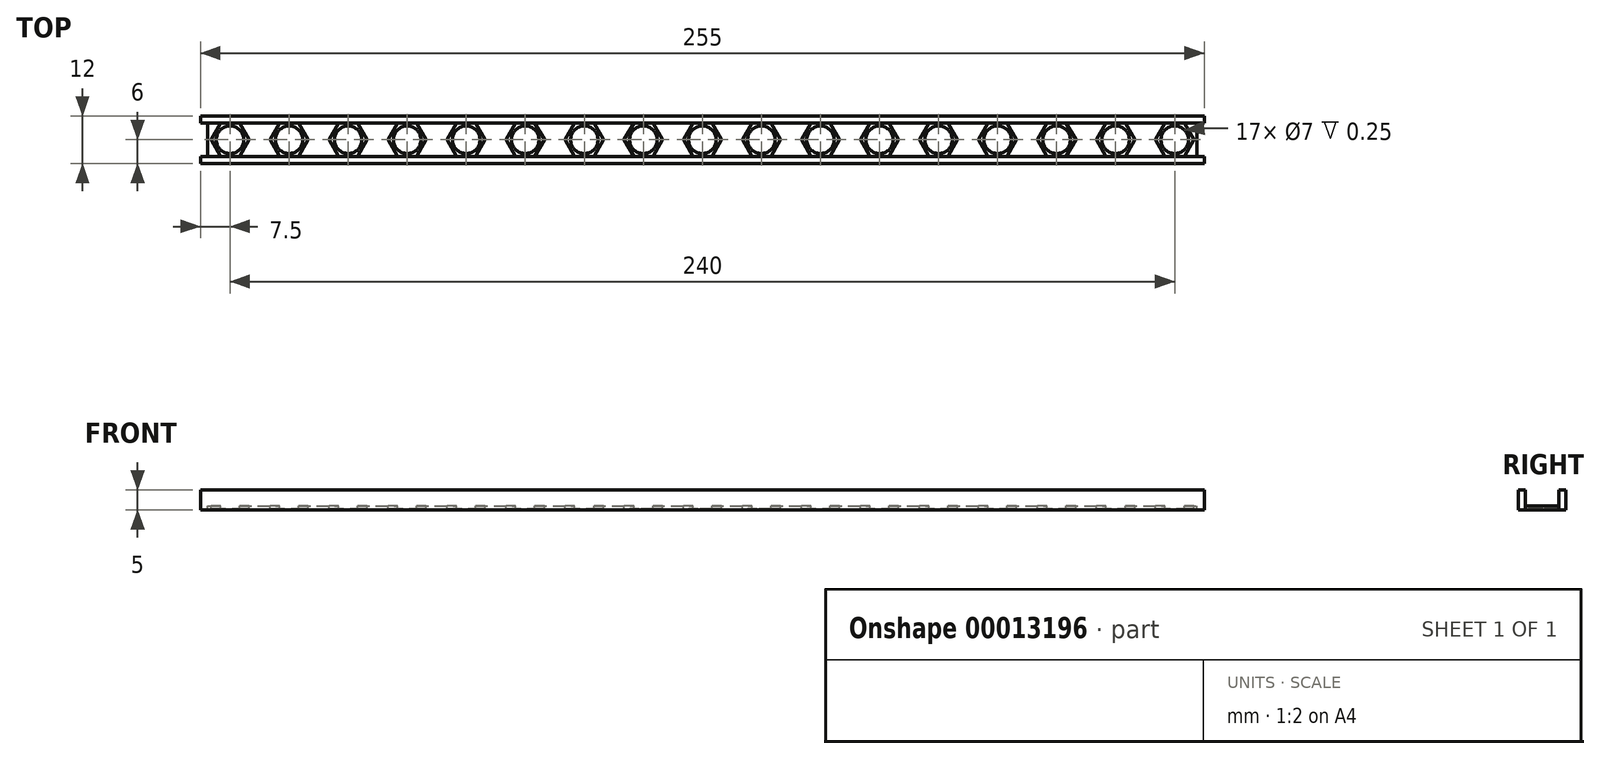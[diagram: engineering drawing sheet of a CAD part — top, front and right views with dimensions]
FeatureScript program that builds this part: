
annotation { "Feature Type Name" : "Feature", "Feature Type Description" : "" }
export const myFeature = defineFeature(function(context is Context, id is Id, definition is map)
    precondition{}
    {
        {
            var Q0;
            Q0=qCreatedBy(makeId("Top.planeOp"),FACE);
            var sketch = newSketch(context, id + "F0", { "sketchPlane" : qUnion([Q0])});
            skLineSegment(sketch, "E0.bottom", {"start": v(-127.5, 6) * mm, "end": v(127.5, 6) * mm});
            skLineSegment(sketch, "E0.top", {"start": v(-127.5, -6) * mm, "end": v(127.5, -6) * mm});
            skLineSegment(sketch, "E0.left", {"start": v(-127.5, 6) * mm, "end": v(-127.5, -6) * mm});
            skLineSegment(sketch, "E0.right", {"start": v(127.5, 6) * mm, "end": v(127.5, -6) * mm});
            skLineSegment(sketch, "E1", {"start": v(0, 0) * mm, "end": v(0, -6) * mm, "construction": true});
            skLineSegment(sketch, "E2", {"start": v(0, 0) * mm, "end": v(127.5, 0) * mm, "construction": true});
            skCircle(sketch, "E3.cCircle", {"center": v(0, 0) * mm, "radius": 4.2 * mm, "construction": true});
            skLineSegment(sketch, "E3.0", {"start": v(2.42, -4.2) * mm, "end": v(-2.42, -4.2) * mm});
            skLineSegment(sketch, "E3.1", {"start": v(-2.42, -4.2) * mm, "end": v(-4.85, 0) * mm});
            skLineSegment(sketch, "E3.2", {"start": v(-4.85, 0) * mm, "end": v(-2.42, 4.2) * mm});
            skLineSegment(sketch, "E3.3", {"start": v(-2.42, 4.2) * mm, "end": v(2.42, 4.2) * mm});
            skLineSegment(sketch, "E3.4", {"start": v(2.42, 4.2) * mm, "end": v(4.85, 0) * mm});
            skLineSegment(sketch, "E3.5", {"start": v(4.85, 0) * mm, "end": v(2.42, -4.2) * mm});
            skPoint(sketch, "E3.0.midPoint", {"position": v(0, -4.2) * mm});
            skCircle(sketch, "E4.cCircle", {"center": v(15, 0) * mm, "radius": 4.2 * mm, "construction": true});
            skLineSegment(sketch, "E4.0", {"start": v(17.42, -4.2) * mm, "end": v(12.58, -4.2) * mm});
            skLineSegment(sketch, "E4.1", {"start": v(12.58, -4.2) * mm, "end": v(10.15, 0) * mm});
            skLineSegment(sketch, "E4.2", {"start": v(10.15, 0) * mm, "end": v(12.58, 4.2) * mm});
            skLineSegment(sketch, "E4.3", {"start": v(12.58, 4.2) * mm, "end": v(17.42, 4.2) * mm});
            skLineSegment(sketch, "E4.4", {"start": v(17.42, 4.2) * mm, "end": v(19.85, 0) * mm});
            skLineSegment(sketch, "E4.5", {"start": v(19.85, 0) * mm, "end": v(17.42, -4.2) * mm});
            skPoint(sketch, "E4.0.midPoint", {"position": v(15, -4.2) * mm});
            skCircle(sketch, "E5.cCircle", {"center": v(-15, 0) * mm, "radius": 4.2 * mm, "construction": true});
            skLineSegment(sketch, "E5.0", {"start": v(-12.58, -4.2) * mm, "end": v(-17.42, -4.2) * mm});
            skLineSegment(sketch, "E5.1", {"start": v(-17.42, -4.2) * mm, "end": v(-19.85, 0) * mm});
            skLineSegment(sketch, "E5.2", {"start": v(-19.85, 0) * mm, "end": v(-17.42, 4.2) * mm});
            skLineSegment(sketch, "E5.3", {"start": v(-17.42, 4.2) * mm, "end": v(-12.58, 4.2) * mm});
            skLineSegment(sketch, "E5.4", {"start": v(-12.58, 4.2) * mm, "end": v(-10.15, 0) * mm});
            skLineSegment(sketch, "E5.5", {"start": v(-10.15, 0) * mm, "end": v(-12.58, -4.2) * mm});
            skPoint(sketch, "E5.0.midPoint", {"position": v(-15, -4.2) * mm});
            skLineSegment(sketch, "E6", {"start": v(-15, 0) * mm, "end": v(0, 0) * mm, "construction": true});
            skLineSegment(sketch, "E7", {"start": v(0, 0) * mm, "end": v(15, 0) * mm, "construction": true});
            skCircle(sketch, "E8", {"center": v(-15, 0) * mm, "radius": 3.5 * mm});
            skCircle(sketch, "E9", {"center": v(0, 0) * mm, "radius": 3.5 * mm});
            skCircle(sketch, "E10", {"center": v(15, 0) * mm, "radius": 3.5 * mm});
            skLineSegment(sketch, "E11.top", {"start": v(-127.5, 4.2) * mm, "end": v(127.5, 4.2) * mm});
            skLineSegment(sketch, "E11.left", {"start": v(-127.5, 6) * mm, "end": v(-127.5, 4.2) * mm});
            skLineSegment(sketch, "E11.right", {"start": v(127.5, 6) * mm, "end": v(127.5, 4.2) * mm});
            skLineSegment(sketch, "E12.top", {"start": v(-127.5, -4.2) * mm, "end": v(127.5, -4.2) * mm});
            skLineSegment(sketch, "E12.left", {"start": v(-127.5, -6) * mm, "end": v(-127.5, -4.2) * mm});
            skLineSegment(sketch, "E12.right", {"start": v(127.5, -6) * mm, "end": v(127.5, -4.2) * mm});
            skLineSegment(sketch, "E13.bottom", {"start": v(-127.5, 4.2) * mm, "end": v(-125.7, 4.2) * mm});
            skLineSegment(sketch, "E13.top", {"start": v(-127.5, -4.2) * mm, "end": v(-125.7, -4.2) * mm});
            skLineSegment(sketch, "E13.left", {"start": v(-127.5, 4.2) * mm, "end": v(-127.5, -4.2) * mm});
            skLineSegment(sketch, "E13.right", {"start": v(-125.7, 4.2) * mm, "end": v(-125.7, -4.2) * mm});
            skLineSegment(sketch, "E14.bottom", {"start": v(127.5, 4.2) * mm, "end": v(125.7, 4.2) * mm});
            skLineSegment(sketch, "E14.top", {"start": v(127.5, -4.2) * mm, "end": v(125.7, -4.2) * mm});
            skLineSegment(sketch, "E14.left", {"start": v(127.5, 4.2) * mm, "end": v(127.5, -4.2) * mm});
            skLineSegment(sketch, "E14.right", {"start": v(125.7, 4.2) * mm, "end": v(125.7, -4.2) * mm});
            skLineSegment(sketch, "E15.1", {"start": v(-32.42, -4.2) * mm, "end": v(-34.85, 0) * mm});
            skCircle(sketch, "E15.cCircle", {"center": v(-30, 0) * mm, "radius": 4.2 * mm, "construction": true});
            skPoint(sketch, "E15.0.midPoint", {"position": v(-30, -4.2) * mm});
            skLineSegment(sketch, "E15.4", {"start": v(-27.58, 4.2) * mm, "end": v(-25.15, 0) * mm});
            skLineSegment(sketch, "E15.2", {"start": v(-34.85, 0) * mm, "end": v(-32.42, 4.2) * mm});
            skLineSegment(sketch, "E15.0", {"start": v(-27.58, -4.2) * mm, "end": v(-32.42, -4.2) * mm});
            skLineSegment(sketch, "E15.3", {"start": v(-32.42, 4.2) * mm, "end": v(-27.58, 4.2) * mm});
            skLineSegment(sketch, "E15.5", {"start": v(-25.15, 0) * mm, "end": v(-27.58, -4.2) * mm});
            skCircle(sketch, "E16", {"center": v(-30, 0) * mm, "radius": 3.5 * mm});
            skLineSegment(sketch, "E17", {"start": v(-30, 0) * mm, "end": v(-15, 0) * mm, "construction": true});
            skLineSegment(sketch, "E18.1", {"start": v(-47.42, -4.2) * mm, "end": v(-49.85, 0) * mm});
            skCircle(sketch, "E18.cCircle", {"center": v(-45, 0) * mm, "radius": 4.2 * mm, "construction": true});
            skPoint(sketch, "E18.0.midPoint", {"position": v(-45, -4.2) * mm});
            skLineSegment(sketch, "E18.4", {"start": v(-42.58, 4.2) * mm, "end": v(-40.15, 0) * mm});
            skLineSegment(sketch, "E18.2", {"start": v(-49.85, 0) * mm, "end": v(-47.42, 4.2) * mm});
            skLineSegment(sketch, "E18.0", {"start": v(-42.58, -4.2) * mm, "end": v(-47.42, -4.2) * mm});
            skLineSegment(sketch, "E18.3", {"start": v(-47.42, 4.2) * mm, "end": v(-42.58, 4.2) * mm});
            skLineSegment(sketch, "E18.5", {"start": v(-40.15, 0) * mm, "end": v(-42.58, -4.2) * mm});
            skCircle(sketch, "E19", {"center": v(-45, 0) * mm, "radius": 3.5 * mm});
            skLineSegment(sketch, "E20", {"start": v(-45, 0) * mm, "end": v(-30, 0) * mm, "construction": true});
            skLineSegment(sketch, "E21.1", {"start": v(-62.42, -4.2) * mm, "end": v(-64.85, 0) * mm});
            skCircle(sketch, "E21.cCircle", {"center": v(-60, 0) * mm, "radius": 4.2 * mm, "construction": true});
            skPoint(sketch, "E21.0.midPoint", {"position": v(-60, -4.2) * mm});
            skLineSegment(sketch, "E21.4", {"start": v(-57.58, 4.2) * mm, "end": v(-55.15, 0) * mm});
            skLineSegment(sketch, "E21.2", {"start": v(-64.85, 0) * mm, "end": v(-62.42, 4.2) * mm});
            skLineSegment(sketch, "E21.0", {"start": v(-57.58, -4.2) * mm, "end": v(-62.42, -4.2) * mm});
            skLineSegment(sketch, "E21.3", {"start": v(-62.42, 4.2) * mm, "end": v(-57.58, 4.2) * mm});
            skLineSegment(sketch, "E21.5", {"start": v(-55.15, 0) * mm, "end": v(-57.58, -4.2) * mm});
            skCircle(sketch, "E22", {"center": v(-60, 0) * mm, "radius": 3.5 * mm});
            skLineSegment(sketch, "E23", {"start": v(-60, 0) * mm, "end": v(-45, 0) * mm, "construction": true});
            skLineSegment(sketch, "E24.1", {"start": v(-77.42, -4.2) * mm, "end": v(-79.85, 0) * mm});
            skCircle(sketch, "E24.cCircle", {"center": v(-75, 0) * mm, "radius": 4.2 * mm, "construction": true});
            skPoint(sketch, "E24.0.midPoint", {"position": v(-75, -4.2) * mm});
            skLineSegment(sketch, "E24.4", {"start": v(-72.58, 4.2) * mm, "end": v(-70.15, 0) * mm});
            skLineSegment(sketch, "E24.2", {"start": v(-79.85, 0) * mm, "end": v(-77.42, 4.2) * mm});
            skLineSegment(sketch, "E24.0", {"start": v(-72.58, -4.2) * mm, "end": v(-77.42, -4.2) * mm});
            skLineSegment(sketch, "E24.3", {"start": v(-77.42, 4.2) * mm, "end": v(-72.58, 4.2) * mm});
            skLineSegment(sketch, "E24.5", {"start": v(-70.15, 0) * mm, "end": v(-72.58, -4.2) * mm});
            skCircle(sketch, "E25", {"center": v(-75, 0) * mm, "radius": 3.5 * mm});
            skLineSegment(sketch, "E26", {"start": v(-75, 0) * mm, "end": v(-60, 0) * mm, "construction": true});
            skLineSegment(sketch, "E27.1", {"start": v(-92.42, -4.2) * mm, "end": v(-94.85, 0) * mm});
            skCircle(sketch, "E27.cCircle", {"center": v(-90, 0) * mm, "radius": 4.2 * mm, "construction": true});
            skPoint(sketch, "E27.0.midPoint", {"position": v(-90, -4.2) * mm});
            skLineSegment(sketch, "E27.4", {"start": v(-87.58, 4.2) * mm, "end": v(-85.15, 0) * mm});
            skLineSegment(sketch, "E27.2", {"start": v(-94.85, 0) * mm, "end": v(-92.42, 4.2) * mm});
            skLineSegment(sketch, "E27.0", {"start": v(-87.58, -4.2) * mm, "end": v(-92.42, -4.2) * mm});
            skLineSegment(sketch, "E27.3", {"start": v(-92.42, 4.2) * mm, "end": v(-87.58, 4.2) * mm});
            skLineSegment(sketch, "E27.5", {"start": v(-85.15, 0) * mm, "end": v(-87.58, -4.2) * mm});
            skCircle(sketch, "E28", {"center": v(-90, 0) * mm, "radius": 3.5 * mm});
            skLineSegment(sketch, "E29", {"start": v(-90, 0) * mm, "end": v(-75, 0) * mm, "construction": true});
            skLineSegment(sketch, "E30.1", {"start": v(-107.42, -4.2) * mm, "end": v(-109.85, 0) * mm});
            skCircle(sketch, "E30.cCircle", {"center": v(-105, 0) * mm, "radius": 4.2 * mm, "construction": true});
            skPoint(sketch, "E30.0.midPoint", {"position": v(-105, -4.2) * mm});
            skLineSegment(sketch, "E30.4", {"start": v(-102.58, 4.2) * mm, "end": v(-100.15, 0) * mm});
            skLineSegment(sketch, "E30.2", {"start": v(-109.85, 0) * mm, "end": v(-107.42, 4.2) * mm});
            skLineSegment(sketch, "E30.0", {"start": v(-102.58, -4.2) * mm, "end": v(-107.42, -4.2) * mm});
            skLineSegment(sketch, "E30.3", {"start": v(-107.42, 4.2) * mm, "end": v(-102.58, 4.2) * mm});
            skLineSegment(sketch, "E30.5", {"start": v(-100.15, 0) * mm, "end": v(-102.58, -4.2) * mm});
            skCircle(sketch, "E31", {"center": v(-105, 0) * mm, "radius": 3.5 * mm});
            skLineSegment(sketch, "E32", {"start": v(-105, 0) * mm, "end": v(-90, 0) * mm, "construction": true});
            skLineSegment(sketch, "E33.1", {"start": v(-122.42, -4.2) * mm, "end": v(-124.85, 0) * mm});
            skCircle(sketch, "E33.cCircle", {"center": v(-120, 0) * mm, "radius": 4.2 * mm, "construction": true});
            skPoint(sketch, "E33.0.midPoint", {"position": v(-120, -4.2) * mm});
            skLineSegment(sketch, "E33.4", {"start": v(-117.58, 4.2) * mm, "end": v(-115.15, 0) * mm});
            skLineSegment(sketch, "E33.2", {"start": v(-124.85, 0) * mm, "end": v(-122.42, 4.2) * mm});
            skLineSegment(sketch, "E33.0", {"start": v(-117.58, -4.2) * mm, "end": v(-122.42, -4.2) * mm});
            skLineSegment(sketch, "E33.3", {"start": v(-122.42, 4.2) * mm, "end": v(-117.58, 4.2) * mm});
            skLineSegment(sketch, "E33.5", {"start": v(-115.15, 0) * mm, "end": v(-117.58, -4.2) * mm});
            skCircle(sketch, "E34", {"center": v(-120, 0) * mm, "radius": 3.5 * mm});
            skLineSegment(sketch, "E35", {"start": v(-120, 0) * mm, "end": v(-105, 0) * mm, "construction": true});
            skLineSegment(sketch, "E36.1", {"start": v(27.58, -4.2) * mm, "end": v(25.15, 0) * mm});
            skCircle(sketch, "E36.cCircle", {"center": v(30, 0) * mm, "radius": 4.2 * mm, "construction": true});
            skPoint(sketch, "E36.0.midPoint", {"position": v(30, -4.2) * mm});
            skLineSegment(sketch, "E36.4", {"start": v(32.42, 4.2) * mm, "end": v(34.85, 0) * mm});
            skLineSegment(sketch, "E36.2", {"start": v(25.15, 0) * mm, "end": v(27.58, 4.2) * mm});
            skLineSegment(sketch, "E36.0", {"start": v(32.42, -4.2) * mm, "end": v(27.58, -4.2) * mm});
            skLineSegment(sketch, "E36.3", {"start": v(27.58, 4.2) * mm, "end": v(32.42, 4.2) * mm});
            skLineSegment(sketch, "E36.5", {"start": v(34.85, 0) * mm, "end": v(32.42, -4.2) * mm});
            skCircle(sketch, "E37", {"center": v(30, 0) * mm, "radius": 3.5 * mm});
            skLineSegment(sketch, "E38", {"start": v(15, 0) * mm, "end": v(30, 0) * mm, "construction": true});
            skLineSegment(sketch, "E39.1", {"start": v(42.58, -4.2) * mm, "end": v(40.15, 0) * mm});
            skCircle(sketch, "E39.cCircle", {"center": v(45, 0) * mm, "radius": 4.2 * mm, "construction": true});
            skPoint(sketch, "E39.0.midPoint", {"position": v(45, -4.2) * mm});
            skLineSegment(sketch, "E39.4", {"start": v(47.42, 4.2) * mm, "end": v(49.85, 0) * mm});
            skLineSegment(sketch, "E39.2", {"start": v(40.15, 0) * mm, "end": v(42.58, 4.2) * mm});
            skLineSegment(sketch, "E39.0", {"start": v(47.42, -4.2) * mm, "end": v(42.58, -4.2) * mm});
            skLineSegment(sketch, "E39.3", {"start": v(42.58, 4.2) * mm, "end": v(47.42, 4.2) * mm});
            skLineSegment(sketch, "E39.5", {"start": v(49.85, 0) * mm, "end": v(47.42, -4.2) * mm});
            skCircle(sketch, "E40", {"center": v(45, 0) * mm, "radius": 3.5 * mm});
            skLineSegment(sketch, "E41", {"start": v(30, 0) * mm, "end": v(45, 0) * mm, "construction": true});
            skLineSegment(sketch, "E42.1", {"start": v(57.58, -4.2) * mm, "end": v(55.15, 0) * mm});
            skCircle(sketch, "E42.cCircle", {"center": v(60, 0) * mm, "radius": 4.2 * mm, "construction": true});
            skPoint(sketch, "E42.0.midPoint", {"position": v(60, -4.2) * mm});
            skLineSegment(sketch, "E42.4", {"start": v(62.42, 4.2) * mm, "end": v(64.85, 0) * mm});
            skLineSegment(sketch, "E42.2", {"start": v(55.15, 0) * mm, "end": v(57.58, 4.2) * mm});
            skLineSegment(sketch, "E42.0", {"start": v(62.42, -4.2) * mm, "end": v(57.58, -4.2) * mm});
            skLineSegment(sketch, "E42.3", {"start": v(57.58, 4.2) * mm, "end": v(62.42, 4.2) * mm});
            skLineSegment(sketch, "E42.5", {"start": v(64.85, 0) * mm, "end": v(62.42, -4.2) * mm});
            skCircle(sketch, "E43", {"center": v(60, 0) * mm, "radius": 3.5 * mm});
            skLineSegment(sketch, "E44", {"start": v(45, 0) * mm, "end": v(60, 0) * mm, "construction": true});
            skLineSegment(sketch, "E45.1", {"start": v(72.58, -4.2) * mm, "end": v(70.15, 0) * mm});
            skCircle(sketch, "E45.cCircle", {"center": v(75, 0) * mm, "radius": 4.2 * mm, "construction": true});
            skPoint(sketch, "E45.0.midPoint", {"position": v(75, -4.2) * mm});
            skLineSegment(sketch, "E45.4", {"start": v(77.42, 4.2) * mm, "end": v(79.85, 0) * mm});
            skLineSegment(sketch, "E45.2", {"start": v(70.15, 0) * mm, "end": v(72.58, 4.2) * mm});
            skLineSegment(sketch, "E45.0", {"start": v(77.42, -4.2) * mm, "end": v(72.58, -4.2) * mm});
            skLineSegment(sketch, "E45.3", {"start": v(72.58, 4.2) * mm, "end": v(77.42, 4.2) * mm});
            skLineSegment(sketch, "E45.5", {"start": v(79.85, 0) * mm, "end": v(77.42, -4.2) * mm});
            skCircle(sketch, "E46", {"center": v(75, 0) * mm, "radius": 3.5 * mm});
            skLineSegment(sketch, "E47", {"start": v(60, 0) * mm, "end": v(75, 0) * mm, "construction": true});
            skLineSegment(sketch, "E48.1", {"start": v(87.58, -4.2) * mm, "end": v(85.15, 0) * mm});
            skCircle(sketch, "E48.cCircle", {"center": v(90, 0) * mm, "radius": 4.2 * mm, "construction": true});
            skPoint(sketch, "E48.0.midPoint", {"position": v(90, -4.2) * mm});
            skLineSegment(sketch, "E48.4", {"start": v(92.42, 4.2) * mm, "end": v(94.85, 0) * mm});
            skLineSegment(sketch, "E48.2", {"start": v(85.15, 0) * mm, "end": v(87.58, 4.2) * mm});
            skLineSegment(sketch, "E48.0", {"start": v(92.42, -4.2) * mm, "end": v(87.58, -4.2) * mm});
            skLineSegment(sketch, "E48.3", {"start": v(87.58, 4.2) * mm, "end": v(92.42, 4.2) * mm});
            skLineSegment(sketch, "E48.5", {"start": v(94.85, 0) * mm, "end": v(92.42, -4.2) * mm});
            skCircle(sketch, "E49", {"center": v(90, 0) * mm, "radius": 3.5 * mm});
            skLineSegment(sketch, "E50", {"start": v(75, 0) * mm, "end": v(90, 0) * mm, "construction": true});
            skLineSegment(sketch, "E51.1", {"start": v(102.58, -4.2) * mm, "end": v(100.15, 0) * mm});
            skCircle(sketch, "E51.cCircle", {"center": v(105, 0) * mm, "radius": 4.2 * mm, "construction": true});
            skPoint(sketch, "E51.0.midPoint", {"position": v(105, -4.2) * mm});
            skLineSegment(sketch, "E51.4", {"start": v(107.42, 4.2) * mm, "end": v(109.85, 0) * mm});
            skLineSegment(sketch, "E51.2", {"start": v(100.15, 0) * mm, "end": v(102.58, 4.2) * mm});
            skLineSegment(sketch, "E51.0", {"start": v(107.42, -4.2) * mm, "end": v(102.58, -4.2) * mm});
            skLineSegment(sketch, "E51.3", {"start": v(102.58, 4.2) * mm, "end": v(107.42, 4.2) * mm});
            skLineSegment(sketch, "E51.5", {"start": v(109.85, 0) * mm, "end": v(107.42, -4.2) * mm});
            skCircle(sketch, "E52", {"center": v(105, 0) * mm, "radius": 3.5 * mm});
            skLineSegment(sketch, "E53", {"start": v(90, 0) * mm, "end": v(105, 0) * mm, "construction": true});
            skLineSegment(sketch, "E54.1", {"start": v(117.58, -4.2) * mm, "end": v(115.15, 0) * mm});
            skCircle(sketch, "E54.cCircle", {"center": v(120, 0) * mm, "radius": 4.2 * mm, "construction": true});
            skPoint(sketch, "E54.0.midPoint", {"position": v(120, -4.2) * mm});
            skLineSegment(sketch, "E54.4", {"start": v(122.42, 4.2) * mm, "end": v(124.85, 0) * mm});
            skLineSegment(sketch, "E54.2", {"start": v(115.15, 0) * mm, "end": v(117.58, 4.2) * mm});
            skLineSegment(sketch, "E54.0", {"start": v(122.42, -4.2) * mm, "end": v(117.58, -4.2) * mm});
            skLineSegment(sketch, "E54.3", {"start": v(117.58, 4.2) * mm, "end": v(122.42, 4.2) * mm});
            skLineSegment(sketch, "E54.5", {"start": v(124.85, 0) * mm, "end": v(122.42, -4.2) * mm});
            skCircle(sketch, "E55", {"center": v(120, 0) * mm, "radius": 3.5 * mm});
            skLineSegment(sketch, "E56", {"start": v(105, 0) * mm, "end": v(120, 0) * mm, "construction": true});
            skSolve(sketch);
        }
        {
            var Q0;
            {var subQ2=sQuery(id+"F0.wireOp",EDGE,"E5.1");Q0=makeQuery(id+"F0.imprint","IMPRINT",FACE,{"disambiguationData":[TD([[makeQuery(id+"F0.imprint","IMPRINT",EDGE,{"derivedFrom":subQ2}),1.0]])]});}
            var Q1;
            {var subQ2=sQuery(id+"F0.wireOp",EDGE,"E3.1");Q1=makeQuery(id+"F0.imprint","IMPRINT",FACE,{"disambiguationData":[TD([[makeQuery(id+"F0.imprint","IMPRINT",EDGE,{"derivedFrom":subQ2}),1.0]])]});}
            var Q2;
            {var subQ5=sQuery(id+"F0.wireOp",EDGE,"E3.4");Q2=makeQuery(id+"F0.imprint","IMPRINT",FACE,{"disambiguationData":[TD([[makeQuery(id+"F0.imprint","IMPRINT",EDGE,{"derivedFrom":subQ5}),1.0]])]});}
            var Q3;
            {var subQ4=sQuery(id+"F0.wireOp",EDGE,"E4.4");Q3=makeQuery(id+"F0.imprint","IMPRINT",FACE,{"disambiguationData":[TD([[makeQuery(id+"F0.imprint","IMPRINT",EDGE,{"derivedFrom":subQ4}),1.0]])]});}
            var Q4;
            {var subQ2=sQuery(id+"F0.wireOp",EDGE,"E3.1");Q4=makeQuery(id+"F0.imprint","IMPRINT",FACE,{"disambiguationData":[TD([[makeQuery(id+"F0.imprint","IMPRINT",EDGE,{"derivedFrom":subQ2}),-1.0]])]});}
            var Q5;
            {var subQ2=sQuery(id+"F0.wireOp",EDGE,"E4.1");Q5=makeQuery(id+"F0.imprint","IMPRINT",FACE,{"disambiguationData":[TD([[makeQuery(id+"F0.imprint","IMPRINT",EDGE,{"derivedFrom":subQ2}),-1.0]])]});}
            var Q6;
            {var subQ2=sQuery(id+"F0.wireOp",EDGE,"E5.1");Q6=makeQuery(id+"F0.imprint","IMPRINT",FACE,{"disambiguationData":[TD([[makeQuery(id+"F0.imprint","IMPRINT",EDGE,{"derivedFrom":subQ2}),-1.0]])]});}
            var Q7;
            Q7=makeQuery(id+"F0.imprint","IMPRINT",FACE,{"disambiguationData":[TD([[makeQuery(id+"F0.imprint","IMPRINT",EDGE,{"derivedFrom":sQuery(id+"F0.wireOp",EDGE,"E0.top")}),1.0]])]});
            var Q8;
            Q8=makeQuery(id+"F0.imprint","IMPRINT",FACE,{"disambiguationData":[TD([[makeQuery(id+"F0.imprint","IMPRINT",EDGE,{"derivedFrom":sQuery(id+"F0.wireOp",EDGE,"E13.bottom")}),-1.0]])]});
            var Q9;
            Q9=makeQuery(id+"F0.imprint","IMPRINT",FACE,{"disambiguationData":[TD([[makeQuery(id+"F0.imprint","IMPRINT",EDGE,{"derivedFrom":sQuery(id+"F0.wireOp",EDGE,"E0.bottom")}),-1.0]])]});
            var Q10;
            Q10=makeQuery(id+"F0.imprint","IMPRINT",FACE,{"disambiguationData":[TD([[makeQuery(id+"F0.imprint","IMPRINT",EDGE,{"derivedFrom":sQuery(id+"F0.wireOp",EDGE,"E14.bottom")}),1.0]])]});
            var Q11;
            {var subQ2=sQuery(id+"F0.wireOp",EDGE,"E13.right");Q11=makeQuery(id+"F0.imprint","IMPRINT",FACE,{"disambiguationData":[TD([[makeQuery(id+"F0.imprint","IMPRINT",EDGE,{"derivedFrom":subQ2}),1.0]])]});}
            var Q12;
            Q12=makeQuery(id+"F0.imprint","IMPRINT",FACE,{"disambiguationData":[TD([[makeQuery(id+"F0.imprint","IMPRINT",EDGE,{"derivedFrom":sQuery(id+"F0.wireOp",EDGE,"E33.1")}),-1.0]])]});
            var Q13;
            {var subQ3=sQuery(id+"F0.wireOp",EDGE,"E30.1");Q13=makeQuery(id+"F0.imprint","IMPRINT",FACE,{"disambiguationData":[TD([[makeQuery(id+"F0.imprint","IMPRINT",EDGE,{"derivedFrom":subQ3}),1.0]])]});}
            var Q14;
            Q14=makeQuery(id+"F0.imprint","IMPRINT",FACE,{"disambiguationData":[TD([[makeQuery(id+"F0.imprint","IMPRINT",EDGE,{"derivedFrom":sQuery(id+"F0.wireOp",EDGE,"E30.1")}),-1.0]])]});
            var Q15;
            {var subQ3=sQuery(id+"F0.wireOp",EDGE,"E27.1");Q15=makeQuery(id+"F0.imprint","IMPRINT",FACE,{"disambiguationData":[TD([[makeQuery(id+"F0.imprint","IMPRINT",EDGE,{"derivedFrom":subQ3}),1.0]])]});}
            var Q16;
            Q16=makeQuery(id+"F0.imprint","IMPRINT",FACE,{"disambiguationData":[TD([[makeQuery(id+"F0.imprint","IMPRINT",EDGE,{"derivedFrom":sQuery(id+"F0.wireOp",EDGE,"E27.1")}),-1.0]])]});
            var Q17;
            {var subQ3=sQuery(id+"F0.wireOp",EDGE,"E24.1");Q17=makeQuery(id+"F0.imprint","IMPRINT",FACE,{"disambiguationData":[TD([[makeQuery(id+"F0.imprint","IMPRINT",EDGE,{"derivedFrom":subQ3}),1.0]])]});}
            var Q18;
            Q18=makeQuery(id+"F0.imprint","IMPRINT",FACE,{"disambiguationData":[TD([[makeQuery(id+"F0.imprint","IMPRINT",EDGE,{"derivedFrom":sQuery(id+"F0.wireOp",EDGE,"E24.1")}),-1.0]])]});
            var Q19;
            {var subQ3=sQuery(id+"F0.wireOp",EDGE,"E21.1");Q19=makeQuery(id+"F0.imprint","IMPRINT",FACE,{"disambiguationData":[TD([[makeQuery(id+"F0.imprint","IMPRINT",EDGE,{"derivedFrom":subQ3}),1.0]])]});}
            var Q20;
            Q20=makeQuery(id+"F0.imprint","IMPRINT",FACE,{"disambiguationData":[TD([[makeQuery(id+"F0.imprint","IMPRINT",EDGE,{"derivedFrom":sQuery(id+"F0.wireOp",EDGE,"E21.1")}),-1.0]])]});
            var Q21;
            {var subQ1=sQuery(id+"F0.wireOp",EDGE,"E18.1");Q21=makeQuery(id+"F0.imprint","IMPRINT",FACE,{"disambiguationData":[TD([[makeQuery(id+"F0.imprint","IMPRINT",EDGE,{"derivedFrom":subQ1}),1.0]])]});}
            var Q22;
            Q22=makeQuery(id+"F0.imprint","IMPRINT",FACE,{"disambiguationData":[TD([[makeQuery(id+"F0.imprint","IMPRINT",EDGE,{"derivedFrom":sQuery(id+"F0.wireOp",EDGE,"E18.1")}),-1.0]])]});
            var Q23;
            {var subQ3=sQuery(id+"F0.wireOp",EDGE,"E15.1");Q23=makeQuery(id+"F0.imprint","IMPRINT",FACE,{"disambiguationData":[TD([[makeQuery(id+"F0.imprint","IMPRINT",EDGE,{"derivedFrom":subQ3}),1.0]])]});}
            var Q24;
            Q24=makeQuery(id+"F0.imprint","IMPRINT",FACE,{"disambiguationData":[TD([[makeQuery(id+"F0.imprint","IMPRINT",EDGE,{"derivedFrom":sQuery(id+"F0.wireOp",EDGE,"E15.1")}),-1.0]])]});
            var Q25;
            {var subQ3=sQuery(id+"F0.wireOp",EDGE,"E14.right");Q25=makeQuery(id+"F0.imprint","IMPRINT",FACE,{"disambiguationData":[TD([[makeQuery(id+"F0.imprint","IMPRINT",EDGE,{"derivedFrom":subQ3}),-1.0]])]});}
            var Q26;
            {var subQ3=sQuery(id+"F0.wireOp",EDGE,"E51.4");Q26=makeQuery(id+"F0.imprint","IMPRINT",FACE,{"disambiguationData":[TD([[makeQuery(id+"F0.imprint","IMPRINT",EDGE,{"derivedFrom":subQ3}),1.0]])]});}
            var Q27;
            {var subQ3=sQuery(id+"F0.wireOp",EDGE,"E48.4");Q27=makeQuery(id+"F0.imprint","IMPRINT",FACE,{"disambiguationData":[TD([[makeQuery(id+"F0.imprint","IMPRINT",EDGE,{"derivedFrom":subQ3}),1.0]])]});}
            var Q28;
            {var subQ3=sQuery(id+"F0.wireOp",EDGE,"E45.4");Q28=makeQuery(id+"F0.imprint","IMPRINT",FACE,{"disambiguationData":[TD([[makeQuery(id+"F0.imprint","IMPRINT",EDGE,{"derivedFrom":subQ3}),1.0]])]});}
            var Q29;
            {var subQ2=sQuery(id+"F0.wireOp",EDGE,"E42.4");Q29=makeQuery(id+"F0.imprint","IMPRINT",FACE,{"disambiguationData":[TD([[makeQuery(id+"F0.imprint","IMPRINT",EDGE,{"derivedFrom":subQ2}),1.0]])]});}
            var Q30;
            {var subQ3=sQuery(id+"F0.wireOp",EDGE,"E39.4");Q30=makeQuery(id+"F0.imprint","IMPRINT",FACE,{"disambiguationData":[TD([[makeQuery(id+"F0.imprint","IMPRINT",EDGE,{"derivedFrom":subQ3}),1.0]])]});}
            var Q31;
            {var subQ2=sQuery(id+"F0.wireOp",EDGE,"E36.4");Q31=makeQuery(id+"F0.imprint","IMPRINT",FACE,{"disambiguationData":[TD([[makeQuery(id+"F0.imprint","IMPRINT",EDGE,{"derivedFrom":subQ2}),1.0]])]});}
            var Q32;
            Q32=makeQuery(id+"F0.imprint","IMPRINT",FACE,{"disambiguationData":[TD([[makeQuery(id+"F0.imprint","IMPRINT",EDGE,{"derivedFrom":sQuery(id+"F0.wireOp",EDGE,"E36.1")}),-1.0]])]});
            var Q33;
            Q33=makeQuery(id+"F0.imprint","IMPRINT",FACE,{"disambiguationData":[TD([[makeQuery(id+"F0.imprint","IMPRINT",EDGE,{"derivedFrom":sQuery(id+"F0.wireOp",EDGE,"E39.1")}),-1.0]])]});
            var Q34;
            Q34=makeQuery(id+"F0.imprint","IMPRINT",FACE,{"disambiguationData":[TD([[makeQuery(id+"F0.imprint","IMPRINT",EDGE,{"derivedFrom":sQuery(id+"F0.wireOp",EDGE,"E42.1")}),-1.0]])]});
            var Q35;
            Q35=makeQuery(id+"F0.imprint","IMPRINT",FACE,{"disambiguationData":[TD([[makeQuery(id+"F0.imprint","IMPRINT",EDGE,{"derivedFrom":sQuery(id+"F0.wireOp",EDGE,"E45.1")}),-1.0]])]});
            var Q36;
            Q36=makeQuery(id+"F0.imprint","IMPRINT",FACE,{"disambiguationData":[TD([[makeQuery(id+"F0.imprint","IMPRINT",EDGE,{"derivedFrom":sQuery(id+"F0.wireOp",EDGE,"E48.1")}),-1.0]])]});
            var Q37;
            Q37=makeQuery(id+"F0.imprint","IMPRINT",FACE,{"disambiguationData":[TD([[makeQuery(id+"F0.imprint","IMPRINT",EDGE,{"derivedFrom":sQuery(id+"F0.wireOp",EDGE,"E51.1")}),-1.0]])]});
            var Q38;
            Q38=makeQuery(id+"F0.imprint","IMPRINT",FACE,{"disambiguationData":[TD([[makeQuery(id+"F0.imprint","IMPRINT",EDGE,{"derivedFrom":sQuery(id+"F0.wireOp",EDGE,"E54.1")}),-1.0]])]});
            extrude(context, id + "F1", {"entities" : qUnion([Q0, Q1, Q2, Q3, Q4, Q5, Q6, Q7, Q8, Q9, Q10, Q11, Q12, Q13, Q14, Q15, Q16, Q17, Q18, Q19, Q20, Q21, Q22, Q23, Q24, Q25, Q26, Q27, Q28, Q29, Q30, Q31, Q32, Q33, Q34, Q35, Q36, Q37, Q38]), "oppositeDirection" : true, "depth" : 1 * mm});
        }
        {
            var Q0;
            {var subQ2=sQuery(id+"F0.wireOp",EDGE,"E5.1");Q0=makeQuery(id+"F0.imprint","IMPRINT",FACE,{"disambiguationData":[TD([[makeQuery(id+"F0.imprint","IMPRINT",EDGE,{"derivedFrom":subQ2}),-1.0]])]});}
            var Q1;
            {var subQ2=sQuery(id+"F0.wireOp",EDGE,"E3.1");Q1=makeQuery(id+"F0.imprint","IMPRINT",FACE,{"disambiguationData":[TD([[makeQuery(id+"F0.imprint","IMPRINT",EDGE,{"derivedFrom":subQ2}),-1.0]])]});}
            var Q2;
            {var subQ2=sQuery(id+"F0.wireOp",EDGE,"E4.1");Q2=makeQuery(id+"F0.imprint","IMPRINT",FACE,{"disambiguationData":[TD([[makeQuery(id+"F0.imprint","IMPRINT",EDGE,{"derivedFrom":subQ2}),-1.0]])]});}
            var Q3;
            Q3=makeQuery(id+"F0.imprint","IMPRINT",FACE,{"disambiguationData":[TD([[makeQuery(id+"F0.imprint","IMPRINT",EDGE,{"derivedFrom":sQuery(id+"F0.wireOp",EDGE,"E36.1")}),-1.0]])]});
            var Q4;
            Q4=makeQuery(id+"F0.imprint","IMPRINT",FACE,{"disambiguationData":[TD([[makeQuery(id+"F0.imprint","IMPRINT",EDGE,{"derivedFrom":sQuery(id+"F0.wireOp",EDGE,"E39.1")}),-1.0]])]});
            var Q5;
            Q5=makeQuery(id+"F0.imprint","IMPRINT",FACE,{"disambiguationData":[TD([[makeQuery(id+"F0.imprint","IMPRINT",EDGE,{"derivedFrom":sQuery(id+"F0.wireOp",EDGE,"E42.1")}),-1.0]])]});
            var Q6;
            Q6=makeQuery(id+"F0.imprint","IMPRINT",FACE,{"disambiguationData":[TD([[makeQuery(id+"F0.imprint","IMPRINT",EDGE,{"derivedFrom":sQuery(id+"F0.wireOp",EDGE,"E45.1")}),-1.0]])]});
            var Q7;
            Q7=makeQuery(id+"F0.imprint","IMPRINT",FACE,{"disambiguationData":[TD([[makeQuery(id+"F0.imprint","IMPRINT",EDGE,{"derivedFrom":sQuery(id+"F0.wireOp",EDGE,"E48.1")}),-1.0]])]});
            var Q8;
            Q8=makeQuery(id+"F0.imprint","IMPRINT",FACE,{"disambiguationData":[TD([[makeQuery(id+"F0.imprint","IMPRINT",EDGE,{"derivedFrom":sQuery(id+"F0.wireOp",EDGE,"E51.1")}),-1.0]])]});
            var Q9;
            Q9=makeQuery(id+"F0.imprint","IMPRINT",FACE,{"disambiguationData":[TD([[makeQuery(id+"F0.imprint","IMPRINT",EDGE,{"derivedFrom":sQuery(id+"F0.wireOp",EDGE,"E54.1")}),-1.0]])]});
            var Q10;
            Q10=makeQuery(id+"F0.imprint","IMPRINT",FACE,{"disambiguationData":[TD([[makeQuery(id+"F0.imprint","IMPRINT",EDGE,{"derivedFrom":sQuery(id+"F0.wireOp",EDGE,"E15.1")}),-1.0]])]});
            var Q11;
            Q11=makeQuery(id+"F0.imprint","IMPRINT",FACE,{"disambiguationData":[TD([[makeQuery(id+"F0.imprint","IMPRINT",EDGE,{"derivedFrom":sQuery(id+"F0.wireOp",EDGE,"E18.1")}),-1.0]])]});
            var Q12;
            Q12=makeQuery(id+"F0.imprint","IMPRINT",FACE,{"disambiguationData":[TD([[makeQuery(id+"F0.imprint","IMPRINT",EDGE,{"derivedFrom":sQuery(id+"F0.wireOp",EDGE,"E21.1")}),-1.0]])]});
            var Q13;
            Q13=makeQuery(id+"F0.imprint","IMPRINT",FACE,{"disambiguationData":[TD([[makeQuery(id+"F0.imprint","IMPRINT",EDGE,{"derivedFrom":sQuery(id+"F0.wireOp",EDGE,"E24.1")}),-1.0]])]});
            var Q14;
            Q14=makeQuery(id+"F0.imprint","IMPRINT",FACE,{"disambiguationData":[TD([[makeQuery(id+"F0.imprint","IMPRINT",EDGE,{"derivedFrom":sQuery(id+"F0.wireOp",EDGE,"E27.1")}),-1.0]])]});
            var Q15;
            Q15=makeQuery(id+"F0.imprint","IMPRINT",FACE,{"disambiguationData":[TD([[makeQuery(id+"F0.imprint","IMPRINT",EDGE,{"derivedFrom":sQuery(id+"F0.wireOp",EDGE,"E30.1")}),-1.0]])]});
            var Q16;
            Q16=makeQuery(id+"F0.imprint","IMPRINT",FACE,{"disambiguationData":[TD([[makeQuery(id+"F0.imprint","IMPRINT",EDGE,{"derivedFrom":sQuery(id+"F0.wireOp",EDGE,"E33.1")}),-1.0]])]});
            var Q17;
            Q17=makeQuery(id+"F1.opExtrude","CAP_FACE",FACE,{"disambiguationData":[OSD([sQuery(id+"F0.wireOp",EDGE,"E0.bottom"),sQuery(id+"F0.wireOp",EDGE,"E0.top"),sQuery(id+"F0.wireOp",EDGE,"E0.left"),sQuery(id+"F0.wireOp",EDGE,"E0.right"),sQuery(id+"F0.wireOp",EDGE,"E8"),sQuery(id+"F0.wireOp",EDGE,"E9"),sQuery(id+"F0.wireOp",EDGE,"E10")])],"isStart":false});
            extrude(context, id + "F2", {"entities" : qUnion([Q0, Q1, Q2, Q3, Q4, Q5, Q6, Q7, Q8, Q9, Q10, Q11, Q12, Q13, Q14, Q15, Q16]), "operationType" : NewBodyOperationType.REMOVE, "endBound" : BoundingType.SYMMETRIC, "oppositeDirection" : true, "depth" : 1.5 * mm, "hasSecondDirection" : true, "secondDirectionBound" : SecondDirectionBoundingType.UP_TO_SURFACE, "secondDirectionOppositeDirection" : false, "secondDirectionBoundEntityFace" : qUnion([Q17]), "secondDirectionDepth" : 3.95 * mm});
        }
        {
            var Q0;
            Q0=makeQuery(id+"F0.imprint","IMPRINT",FACE,{"disambiguationData":[TD([[makeQuery(id+"F0.imprint","IMPRINT",EDGE,{"derivedFrom":sQuery(id+"F0.wireOp",EDGE,"E0.bottom")}),-1.0]])]});
            var Q1;
            Q1=makeQuery(id+"F0.imprint","IMPRINT",FACE,{"disambiguationData":[TD([[makeQuery(id+"F0.imprint","IMPRINT",EDGE,{"derivedFrom":sQuery(id+"F0.wireOp",EDGE,"E13.bottom")}),-1.0]])]});
            var Q2;
            Q2=makeQuery(id+"F0.imprint","IMPRINT",FACE,{"disambiguationData":[TD([[makeQuery(id+"F0.imprint","IMPRINT",EDGE,{"derivedFrom":sQuery(id+"F0.wireOp",EDGE,"E0.top")}),1.0]])]});
            var Q3;
            Q3=makeQuery(id+"F0.imprint","IMPRINT",FACE,{"disambiguationData":[TD([[makeQuery(id+"F0.imprint","IMPRINT",EDGE,{"derivedFrom":sQuery(id+"F0.wireOp",EDGE,"E14.bottom")}),1.0]])]});
            extrude(context, id + "F3", {"entities" : qUnion([Q0, Q1, Q2, Q3]), "operationType" : NewBodyOperationType.ADD, "depth" : 4 * mm});
        }
    });
